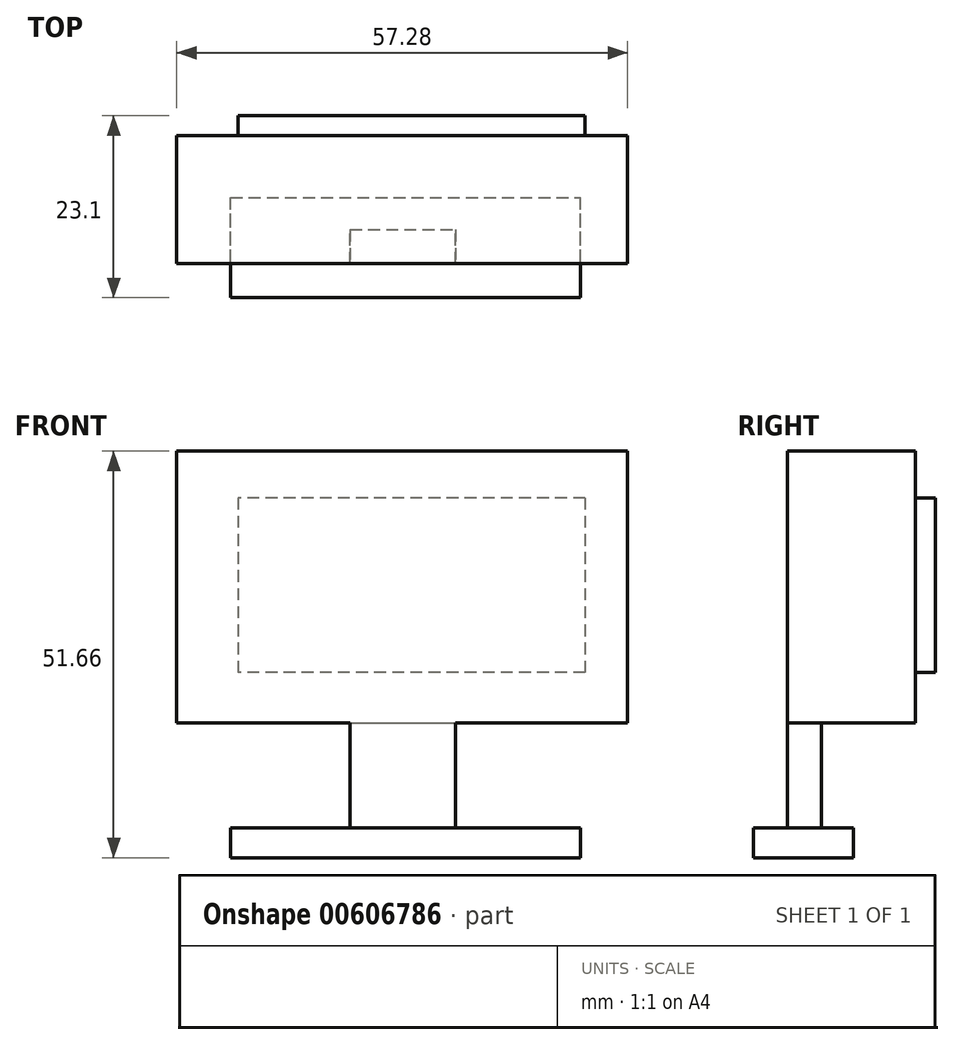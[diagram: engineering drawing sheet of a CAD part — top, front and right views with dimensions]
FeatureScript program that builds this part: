
annotation { "Feature Type Name" : "Feature", "Feature Type Description" : "" }
export const myFeature = defineFeature(function(context is Context, id is Id, definition is map)
    precondition{}
    {
        {
            var Q0;
            Q0=qCreatedBy(makeId("Top.planeOp"),FACE);
            var sketch = newSketch(context, id + "F0", { "sketchPlane" : qUnion([Q0])});
            skLineSegment(sketch, "E0.bottom", {"start": v(-15.17, -20.56) * mm, "end": v(29.28, -20.56) * mm});
            skLineSegment(sketch, "E0.top", {"start": v(-15.17, -7.86) * mm, "end": v(29.28, -7.86) * mm});
            skLineSegment(sketch, "E0.left", {"start": v(-15.17, -20.56) * mm, "end": v(-15.17, -7.86) * mm});
            skLineSegment(sketch, "E0.right", {"start": v(29.28, -20.56) * mm, "end": v(29.28, -7.86) * mm});
            skSolve(sketch);
        }
        {
            var Q0;
            Q0 = qSketchRegion(id + "F0", true);
            extrude(context, id + "F1", {"entities" : qUnion([Q0]), "depth" : 3.8 * mm, "offsetDistance" : 25.4 * mm});
        }
        {
            var Q0;
            Q0=qCreatedBy(makeId("Top.planeOp"),FACE);
            var sketch = newSketch(context, id + "F2", { "sketchPlane" : qUnion([Q0])});
            skLineSegment(sketch, "E1.bottom", {"start": v(0, -11.94) * mm, "end": v(13.38, -11.94) * mm});
            skLineSegment(sketch, "E1.top", {"start": v(0, -16.26) * mm, "end": v(13.38, -16.26) * mm});
            skLineSegment(sketch, "E1.left", {"start": v(0, -11.94) * mm, "end": v(0, -16.26) * mm});
            skLineSegment(sketch, "E1.right", {"start": v(13.38, -11.94) * mm, "end": v(13.38, -16.26) * mm});
            skSolve(sketch);
        }
        {
            var Q0;
            Q0 = qSketchRegion(id + "F2", true);
            extrude(context, id + "F3", {"entities" : qUnion([Q0]), "operationType" : NewBodyOperationType.ADD, "depth" : 50.8 * mm, "offsetDistance" : 25.4 * mm});
        }
        {
            var Q0;
            Q0=qCreatedBy(makeId("Front.planeOp"),FACE);
            var sketch = newSketch(context, id + "F4", { "sketchPlane" : qUnion([Q0])});
            skLineSegment(sketch, "E2.bottom", {"start": v(-22.02, 51.66) * mm, "end": v(35.26, 51.66) * mm});
            skLineSegment(sketch, "E2.top", {"start": v(-22.02, 17.12) * mm, "end": v(35.26, 17.12) * mm});
            skLineSegment(sketch, "E2.left", {"start": v(-22.02, 51.66) * mm, "end": v(-22.02, 17.12) * mm});
            skLineSegment(sketch, "E2.right", {"start": v(35.26, 51.66) * mm, "end": v(35.26, 17.12) * mm});
            skSolve(sketch);
        }
        {
            var Q0;
            Q0 = qSketchRegion(id + "F4", true);
            extrude(context, id + "F5", {"entities" : qUnion([Q0]), "operationType" : NewBodyOperationType.ADD, "depth" : 16.26 * mm, "offsetDistance" : 25.4 * mm});
        }
        {
            var Q0;
            Q0=makeQuery(id+"F5.opExtrude","CAP_FACE",FACE,{"disambiguationData":[OSD([sQuery(id+"F4.wireOp",EDGE,"E2.bottom"),sQuery(id+"F4.wireOp",EDGE,"E2.top"),sQuery(id+"F4.wireOp",EDGE,"E2.left"),sQuery(id+"F4.wireOp",EDGE,"E2.right")])],"isStart":true});
            var sketch = newSketch(context, id + "F6", { "sketchPlane" : qUnion([Q0])});
            skLineSegment(sketch, "E3.bottom", {"start": v(-29.86, 45.73) * mm, "end": v(14.2, 45.73) * mm});
            skLineSegment(sketch, "E3.top", {"start": v(-29.86, 23.55) * mm, "end": v(14.2, 23.55) * mm});
            skLineSegment(sketch, "E3.left", {"start": v(-29.86, 45.73) * mm, "end": v(-29.86, 23.55) * mm});
            skLineSegment(sketch, "E3.right", {"start": v(14.2, 45.73) * mm, "end": v(14.2, 23.55) * mm});
            skSolve(sketch);
        }
        {
            var Q0;
            Q0 = qSketchRegion(id + "F6", true);
            extrude(context, id + "F7", {"entities" : qUnion([Q0]), "operationType" : NewBodyOperationType.ADD, "depth" : 2.54 * mm, "offsetDistance" : 25.4 * mm});
        }
    });
